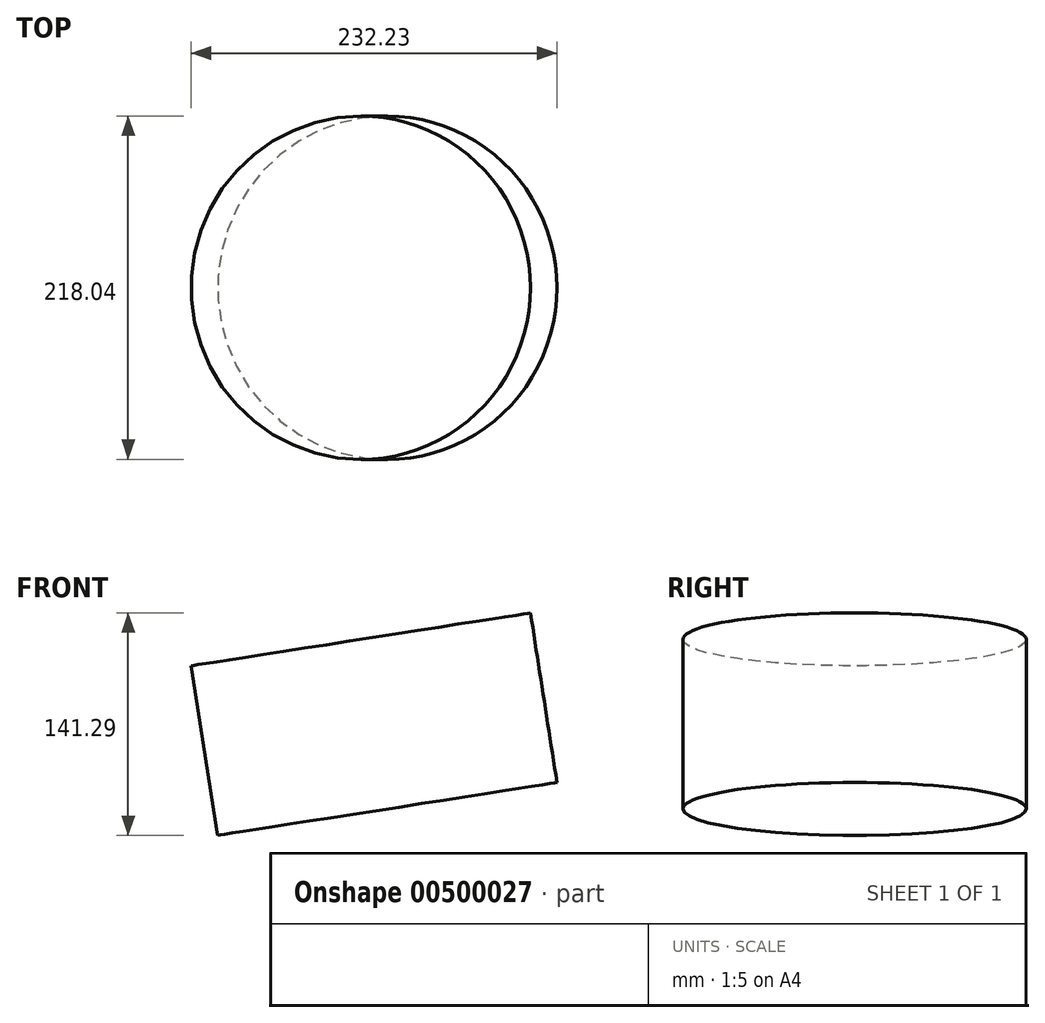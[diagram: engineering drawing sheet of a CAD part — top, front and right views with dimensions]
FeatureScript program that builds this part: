
annotation { "Feature Type Name" : "Feature", "Feature Type Description" : "" }
export const myFeature = defineFeature(function(context is Context, id is Id, definition is map)
    precondition{}
    {
        {
            var Q0;
            Q0=qCreatedBy(makeId("Front.planeOp"),FACE);
            var sketch = newSketch(context, id + "F0", { "sketchPlane" : qUnion([Q0])});
            skCircle(sketch, "E0.cCircle", {"center": v(0, 0) * mm, "radius": 77.1 * mm, "construction": true});
            skLineSegment(sketch, "E0.0", {"start": v(-62.25, 45.47) * mm, "end": v(45.47, 62.25) * mm});
            skLineSegment(sketch, "E0.1", {"start": v(45.47, 62.25) * mm, "end": v(62.25, -45.47) * mm});
            skLineSegment(sketch, "E0.2", {"start": v(62.25, -45.47) * mm, "end": v(-45.47, -62.25) * mm});
            skLineSegment(sketch, "E0.3", {"start": v(-45.47, -62.25) * mm, "end": v(-62.25, 45.47) * mm});
            skSolve(sketch);
        }
        {
            var Q0;
            Q0=makeQuery(id+"F0.imprint","IMPRINT",FACE,{"disambiguationData":[TD([[makeQuery(id+"F0.imprint","IMPRINT",EDGE,{"derivedFrom":sQuery(id+"F0.wireOp",EDGE,"E0.0")}),-1.0]])]});
            var Q1;
            Q1=sQuery(id+"F0.wireOp",EDGE,"E0.1");
            revolve(context, id + "F1", {"entities" : qUnion([Q0]), "axis" : qUnion([Q1]), "revolveType" : RevolveType.FULL});
        }
    });
